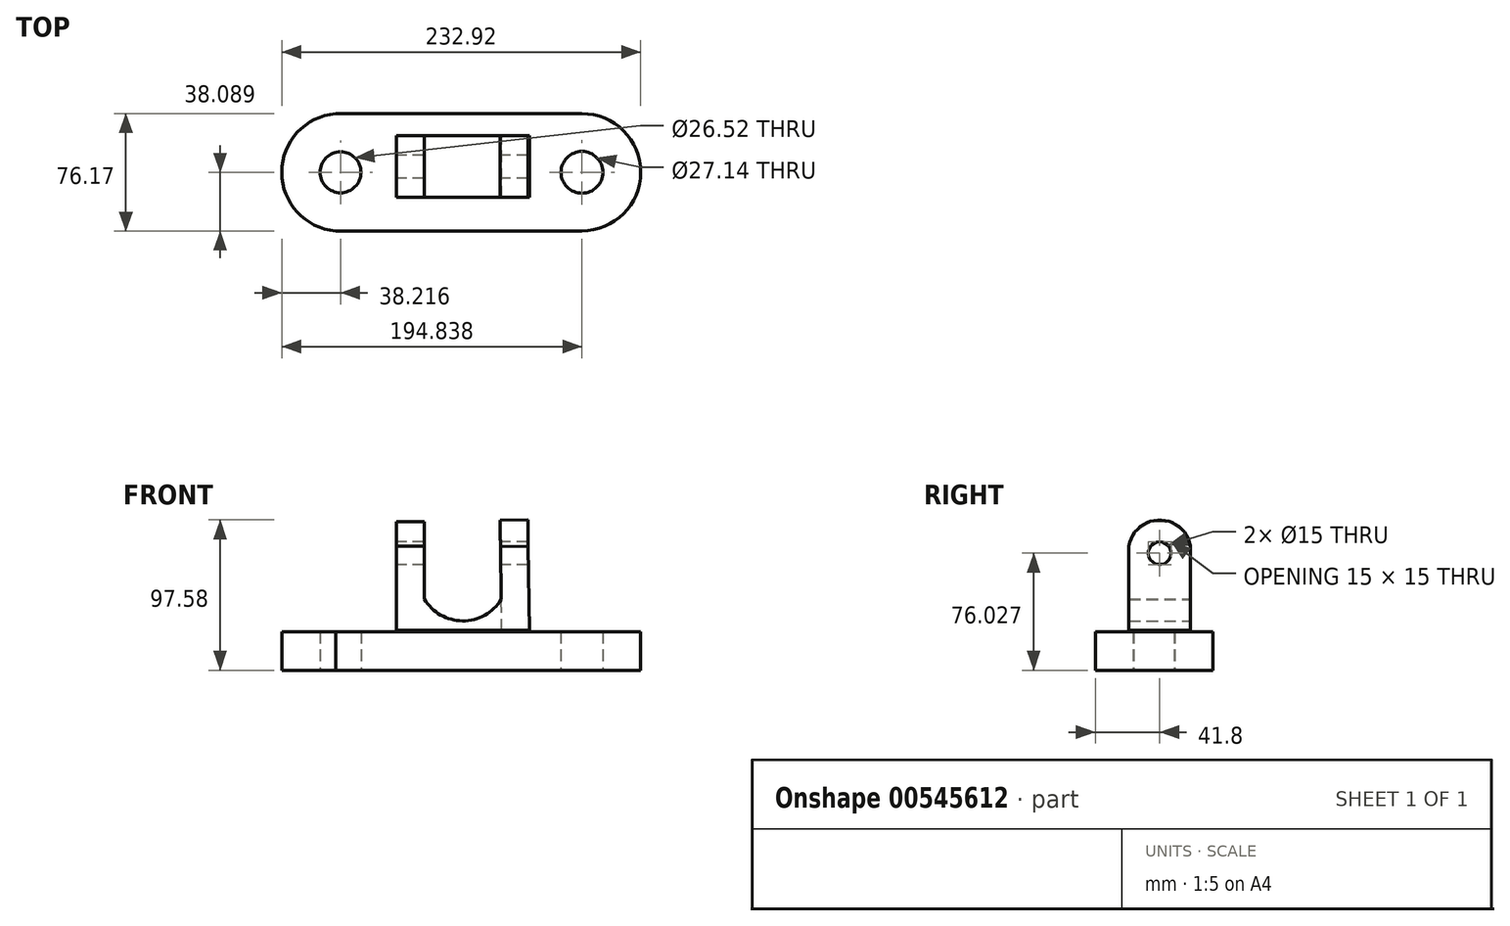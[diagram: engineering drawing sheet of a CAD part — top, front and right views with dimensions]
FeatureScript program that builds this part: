
annotation { "Feature Type Name" : "Feature", "Feature Type Description" : "" }
export const myFeature = defineFeature(function(context is Context, id is Id, definition is map)
    precondition{}
    {
        {
            var Q0;
            Q0=qCreatedBy(makeId("Top.planeOp"),FACE);
            var sketch = newSketch(context, id + "F0", { "sketchPlane" : qUnion([Q0])});
            skLineSegment(sketch, "E0.bottom", {"start": v(-69.44, 29.92) * mm, "end": v(90.35, 29.92) * mm});
            skLineSegment(sketch, "E0.top", {"start": v(-69.44, -46.25) * mm, "end": v(90.35, -46.25) * mm});
            skArc(sketch, "E1", {"start": v(-69.44, 29.92) * mm, "mid": v(-104.5, -8.16) * mm, "end": v(-69.44, -46.25) * mm});
            skArc(sketch, "E2", {"start": v(90.35, -46.25) * mm, "mid": v(128.43, -8.16) * mm, "end": v(90.35, 29.92) * mm});
            skCircle(sketch, "E3", {"center": v(-66.27, -8.16) * mm, "radius": 13.26 * mm});
            skCircle(sketch, "E4", {"center": v(90.35, -8.16) * mm, "radius": 13.57 * mm});
            skSolve(sketch);
        }
        {
            var Q0;
            Q0=makeQuery(id+"F0.imprint","IMPRINT",FACE,{"disambiguationData":[TD([[makeQuery(id+"F0.imprint","IMPRINT",EDGE,{"derivedFrom":sQuery(id+"F0.wireOp",EDGE,"E0.bottom")}),-1.0]])]});
            extrude(context, id + "F1", {"entities" : qUnion([Q0]), "depth" : 25 * mm, "offsetDistance" : 25 * mm});
        }
        {
            var Q0;
            Q0=qCreatedBy(makeId("Front.planeOp"),FACE);
            var sketch = newSketch(context, id + "F2", { "sketchPlane" : qUnion([Q0])});
            skArc(sketch, "E5", {"start": v(-11.93, 46.3) * mm, "mid": v(12.94, 32.1) * mm, "end": v(37.98, 46) * mm});
            skLineSegment(sketch, "E6", {"start": v(-11.93, 46.3) * mm, "end": v(-11.93, 25.85) * mm});
            skLineSegment(sketch, "E7", {"start": v(-11.93, 25.85) * mm, "end": v(38.28, 25.85) * mm});
            skLineSegment(sketch, "E8", {"start": v(38.28, 25.85) * mm, "end": v(37.98, 46) * mm});
            skSolve(sketch);
        }
        {
            var Q0;
            Q0 = qSketchRegion(id + "F2", true);
            extrude(context, id + "F3", {"entities" : qUnion([Q0]), "depth" : 24.5 * mm, "offsetDistance" : 25 * mm});
        }
        {
            var Q0;
            Q0=makeQuery(id+"F3.opExtrude","CAP_FACE",FACE,{"disambiguationData":[OSD([sQuery(id+"F2.wireOp",EDGE,"E5"),sQuery(id+"F2.wireOp",EDGE,"E6"),sQuery(id+"F2.wireOp",EDGE,"E7"),sQuery(id+"F2.wireOp",EDGE,"E8")])],"isStart":true});
            extrude(context, id + "F4", {"entities" : qUnion([Q0]), "operationType" : NewBodyOperationType.ADD, "depth" : 15.6 * mm, "offsetDistance" : 25 * mm});
        }
        {
            var Q0;
            {var subQ0=sQuery(id+"F2.wireOp",EDGE,"E8");Q0=makeQuery(id+"F4.boolean.opBoolean","MERGE",FACE,{"derivedFrom":[makeQuery(id+"F3.opExtrude","SWEPT_FACE",FACE,{"disambiguationData":[OSD([subQ0])]}),makeQuery(id+"F4.opExtrude","SWEPT_FACE",FACE,{"disambiguationData":[OSD([subQ0])]})]});}
            var sketch = newSketch(context, id + "F5", { "sketchPlane" : qUnion([Q0])});
            skLineSegment(sketch, "E9.bottom", {"start": v(-24.5, 25.28) * mm, "end": v(15.49, 25.28) * mm});
            skLineSegment(sketch, "E9.left", {"start": v(-24.5, 25.28) * mm, "end": v(-24.5, 79.86) * mm});
            skLineSegment(sketch, "E9.right", {"start": v(15.49, 25.28) * mm, "end": v(15.49, 79.86) * mm});
            skArc(sketch, "E10", {"start": v(15.49, 79.86) * mm, "mid": v(-4.5, 96.74) * mm, "end": v(-24.5, 79.86) * mm});
            skSolve(sketch);
        }
        {
            var Q0;
            {var subQ0=sQuery(id+"F2.wireOp",EDGE,"E6");Q0=makeQuery(id+"F4.boolean.opBoolean","MERGE",FACE,{"derivedFrom":[makeQuery(id+"F3.opExtrude","SWEPT_FACE",FACE,{"disambiguationData":[OSD([subQ0])]}),makeQuery(id+"F4.opExtrude","SWEPT_FACE",FACE,{"disambiguationData":[OSD([subQ0])]})]});}
            var sketch = newSketch(context, id + "F6", { "sketchPlane" : qUnion([Q0])});
            skLineSegment(sketch, "E11.bottom", {"start": v(-15.6, 25.85) * mm, "end": v(24.5, 25.85) * mm});
            skLineSegment(sketch, "E11.left", {"start": v(-15.6, 25.85) * mm, "end": v(-15.6, 80.47) * mm});
            skLineSegment(sketch, "E11.right", {"start": v(24.5, 25.85) * mm, "end": v(24.5, 80.47) * mm});
            skArc(sketch, "E12", {"start": v(24.5, 80.47) * mm, "mid": v(4.45, 96.56) * mm, "end": v(-15.6, 80.47) * mm});
            skSolve(sketch);
        }
        {
            var Q0;
            {var subQ5=sQuery(id+"F5.wireOp",EDGE,"E10");Q0=makeQuery(id+"F5.imprint","IMPRINT",FACE,{"disambiguationData":[TD([[makeQuery(id+"F5.imprint","IMPRINT",EDGE,{"derivedFrom":subQ5}),1.0]])]});}
            var Q1;
            {var subQ0=sQuery(id+"F5.wireOp",EDGE,"E9.bottom");Q1=makeQuery(id+"F5.imprint","IMPRINT",FACE,{"disambiguationData":[TD([[makeQuery(id+"F5.imprint","IMPRINT",EDGE,{"derivedFrom":subQ0}),1.0]])]});}
            extrude(context, id + "F7", {"entities" : qUnion([Q0, Q1]), "operationType" : NewBodyOperationType.ADD, "depth" : 18 * mm, "offsetDistance" : 25 * mm});
        }
        {
            var Q0;
            {var subQ4=sQuery(id+"F6.wireOp",EDGE,"E12");Q0=makeQuery(id+"F6.imprint","IMPRINT",FACE,{"disambiguationData":[TD([[makeQuery(id+"F6.imprint","IMPRINT",EDGE,{"derivedFrom":subQ4}),1.0]])]});}
            var Q1;
            {var subQ0=sQuery(id+"F6.wireOp",EDGE,"E11.bottom");Q1=makeQuery(id+"F6.imprint","IMPRINT",FACE,{"disambiguationData":[TD([[makeQuery(id+"F6.imprint","IMPRINT",EDGE,{"derivedFrom":subQ0}),-1.0]])]});}
            extrude(context, id + "F8", {"entities" : qUnion([Q0, Q1]), "operationType" : NewBodyOperationType.ADD, "depth" : 18 * mm, "offsetDistance" : 25 * mm});
        }
        {
            var Q0;
            Q0=makeQuery(id+"F8.opExtrude","CAP_FACE",FACE,{"disambiguationData":[OSD([sQuery(id+"F6.wireOp",EDGE,"E11.bottom"),sQuery(id+"F6.wireOp",EDGE,"E11.left"),sQuery(id+"F6.wireOp",EDGE,"E11.right"),sQuery(id+"F6.wireOp",EDGE,"E12")])],"isStart":false});
            var sketch = newSketch(context, id + "F9", { "sketchPlane" : qUnion([Q0])});
            skCircle(sketch, "E13", {"center": v(4.45, 76.03) * mm, "radius": 9.77 * mm});
            skSolve(sketch);
        }
        {
            var Q0;
            Q0=sQuery(id+"F9.wireOp",VERTEX,"E13.center");
            var Q1;
            Q1=makeQuery(id+"F3.opExtrude","SWEPT_BODY",BODY,{"disambiguationData":[OSD([sQuery(id+"F2.wireOp",EDGE,"E5"),sQuery(id+"F2.wireOp",EDGE,"E6"),sQuery(id+"F2.wireOp",EDGE,"E7"),sQuery(id+"F2.wireOp",EDGE,"E8")])]});
            hole(context, id + "F10", {"style" : HoleStyle.SIMPLE, "endStyle" : HoleEndStyle.THROUGH, "holeDiameter" : 15 * mm, "majorDiameter" : 5 * mm, "isTappedThrough" : true, "tappedDepth" : 12 * mm, "tapClearance" : 3, "locations" : qUnion([Q0]), "scope" : qUnion([Q1])});
        }
    });
